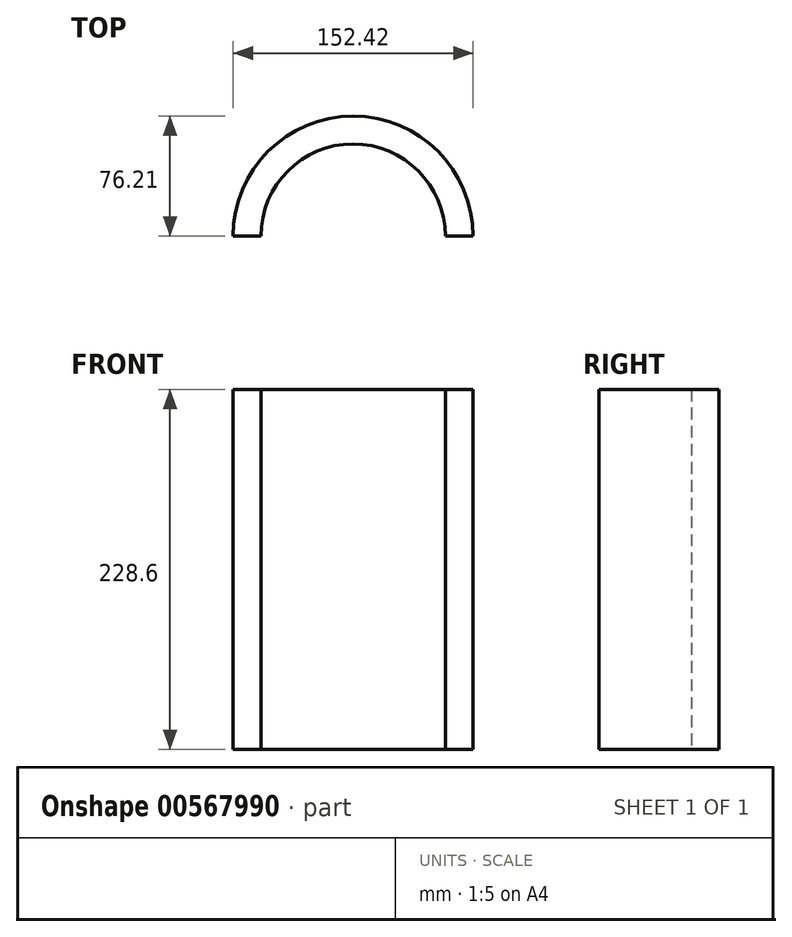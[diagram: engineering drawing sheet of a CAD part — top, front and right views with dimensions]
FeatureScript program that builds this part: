
annotation { "Feature Type Name" : "Feature", "Feature Type Description" : "" }
export const myFeature = defineFeature(function(context is Context, id is Id, definition is map)
    precondition{}
    {
        {
            var Q0;
            Q0=qCreatedBy(makeId("Top.planeOp"),FACE);
            var sketch = newSketch(context, id + "F0", { "sketchPlane" : qUnion([Q0])});
            skCircle(sketch, "E0", {"center": v(0, 0) * mm, "radius": 76.21 * mm});
            skCircle(sketch, "E1", {"center": v(0, 0) * mm, "radius": 58.53 * mm});
            skLineSegment(sketch, "E2", {"start": v(-76.21, 0) * mm, "end": v(76.21, 0) * mm});
            skSolve(sketch);
        }
        {
            var Q0;
            {var subQ0=sQuery(id+"F0.wireOp",EDGE,"E2");var subQ1=sQuery(id+"F0.wireOp",EDGE,"E0");var subQ2=makeQuery(id+"F0.imprint","INTERSECT",VERTEX,{"disambiguationData":[OD(0.0)],"derivedFrom":[subQ1,subQ0]});Q0=makeQuery(id+"F0.imprint","IMPRINT",FACE,{"disambiguationData":[TD([[makeQuery(id+"F0.imprint","IMPRINT",EDGE,{"disambiguationData":[TD([[subQ2,-1.0]])],"derivedFrom":subQ1}),1.0]])]});}
            extrude(context, id + "F1", {"entities" : qUnion([Q0]), "depth" : 228.6 * mm, "offsetDistance" : 25.4 * mm});
        }
    });
